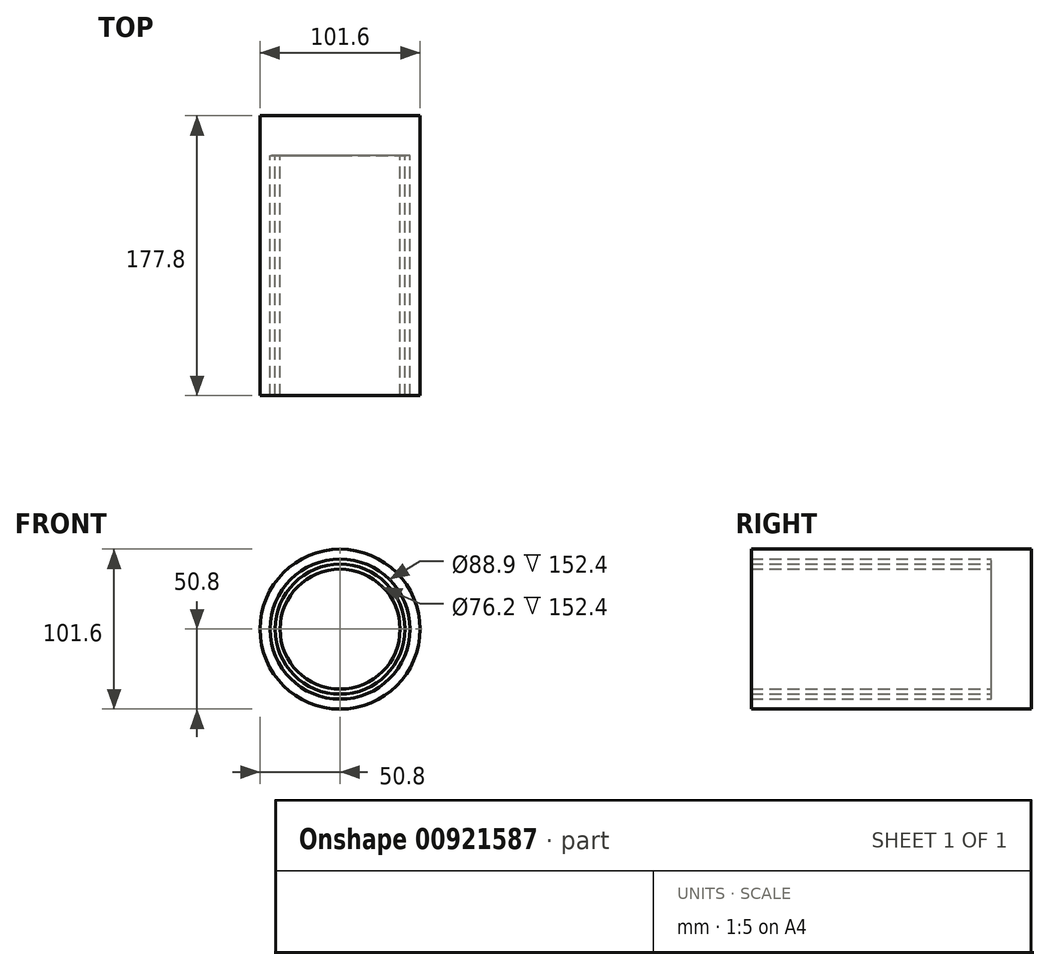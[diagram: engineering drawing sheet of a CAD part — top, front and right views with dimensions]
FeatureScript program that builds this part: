
annotation { "Feature Type Name" : "Feature", "Feature Type Description" : "" }
export const myFeature = defineFeature(function(context is Context, id is Id, definition is map)
    precondition{}
    {
        {
            var Q0;
            Q0=qCreatedBy(makeId("Front.planeOp"),FACE);
            var sketch = newSketch(context, id + "F0", { "sketchPlane" : qUnion([Q0])});
            skCircle(sketch, "E0", {"center": v(0, 0) * mm, "radius": 50.8 * mm});
            skSolve(sketch);
        }
        {
            var Q0;
            Q0 = qSketchRegion(id + "F0", true);
            extrude(context, id + "F1", {"entities" : qUnion([Q0]), "depth" : 25.4 * mm, "offsetDistance" : 25.4 * mm});
        }
        {
            var Q0;
            Q0=makeQuery(id+"F1.opExtrude","CAP_FACE",FACE,{"disambiguationData":[OSD([sQuery(id+"F0.wireOp",EDGE,"E0")])],"isStart":false});
            var sketch = newSketch(context, id + "F2", { "sketchPlane" : qUnion([Q0])});
            skCircle(sketch, "E1", {"center": v(0, 0) * mm, "radius": 50.8 * mm});
            skCircle(sketch, "E2.0", {"center": v(0, 0) * mm, "radius": 44.45 * mm});
            skCircle(sketch, "E3", {"center": v(0, 0) * mm, "radius": 41.28 * mm});
            skCircle(sketch, "E4", {"center": v(0, 0) * mm, "radius": 38.1 * mm});
            skSolve(sketch);
        }
        {
            var Q0;
            Q0=makeQuery(id+"F2.imprint","IMPRINT",FACE,{"disambiguationData":[TD([[makeQuery(id+"F2.imprint","IMPRINT",EDGE,{"derivedFrom":sQuery(id+"F2.wireOp",EDGE,"E1")}),1.0]])]});
            var Q1;
            Q1 = qSketchRegion(id + "F2", true);
            var Q2;
            Q2=makeQuery(id+"F2.imprint","IMPRINT",FACE,{"disambiguationData":[TD([[makeQuery(id+"F2.imprint","IMPRINT",EDGE,{"derivedFrom":sQuery(id+"F2.wireOp",EDGE,"E3")}),1.0]])]});
            extrude(context, id + "F3", {"entities" : qUnion([Q0, Q1, Q2]), "operationType" : NewBodyOperationType.ADD, "depth" : 152.4 * mm, "offsetDistance" : 25.4 * mm});
        }
    });
